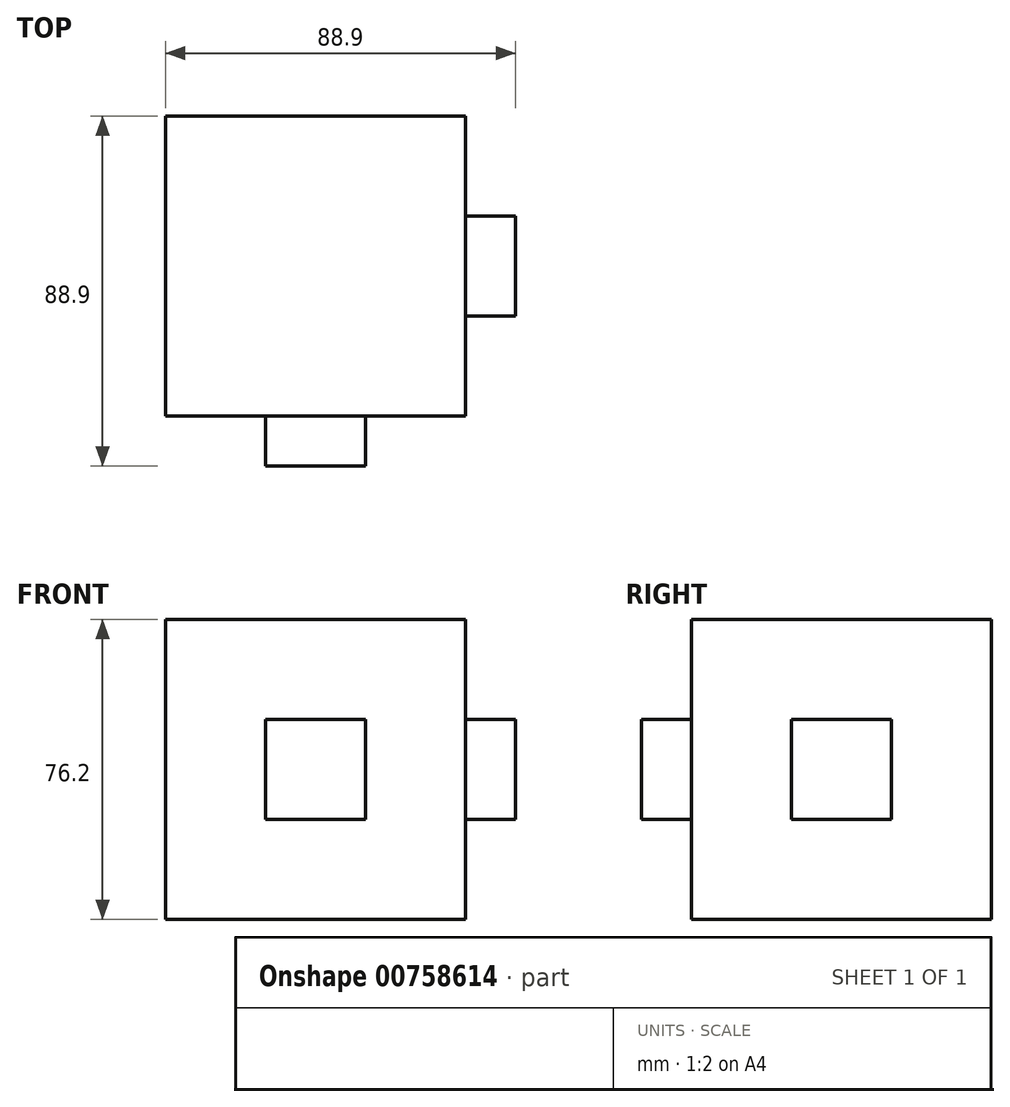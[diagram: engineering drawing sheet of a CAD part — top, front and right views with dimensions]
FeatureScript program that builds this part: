
annotation { "Feature Type Name" : "Feature", "Feature Type Description" : "" }
export const myFeature = defineFeature(function(context is Context, id is Id, definition is map)
    precondition{}
    {
        {
            var Q0;
            Q0=qCreatedBy(makeId("Front.planeOp"),FACE);
            var sketch = newSketch(context, id + "F0", { "sketchPlane" : qUnion([Q0])});
            skLineSegment(sketch, "E0.bottom", {"start": v(-42.26, 44.8) * mm, "end": v(33.94, 44.8) * mm});
            skLineSegment(sketch, "E0.top", {"start": v(-42.26, -31.4) * mm, "end": v(33.94, -31.4) * mm});
            skLineSegment(sketch, "E0.left", {"start": v(-42.26, 44.8) * mm, "end": v(-42.26, -31.4) * mm});
            skLineSegment(sketch, "E0.right", {"start": v(33.94, 44.8) * mm, "end": v(33.94, -31.4) * mm});
            skSolve(sketch);
        }
        {
            var Q0;
            Q0=makeQuery(id+"F0.imprint","IMPRINT",FACE,{"disambiguationData":[TD([[makeQuery(id+"F0.imprint","IMPRINT",EDGE,{"derivedFrom":sQuery(id+"F0.wireOp",EDGE,"E0.bottom")}),-1.0]])]});
            extrude(context, id + "F1", {"entities" : qUnion([Q0]), "depth" : 76.2 * mm, "offsetDistance" : 25.4 * mm});
        }
        {
            var Q0;
            Q0=makeQuery(id+"F1.opExtrude","CAP_FACE",FACE,{"disambiguationData":[OSD([sQuery(id+"F0.wireOp",EDGE,"E0.bottom"),sQuery(id+"F0.wireOp",EDGE,"E0.top"),sQuery(id+"F0.wireOp",EDGE,"E0.left"),sQuery(id+"F0.wireOp",EDGE,"E0.right")])],"isStart":false});
            var sketch = newSketch(context, id + "F2", { "sketchPlane" : qUnion([Q0])});
            skLineSegment(sketch, "E1.bottom", {"start": v(-16.86, 19.4) * mm, "end": v(8.54, 19.4) * mm});
            skLineSegment(sketch, "E1.top", {"start": v(-16.86, -6) * mm, "end": v(8.54, -6) * mm});
            skLineSegment(sketch, "E1.left", {"start": v(-16.86, 19.4) * mm, "end": v(-16.86, -6) * mm});
            skLineSegment(sketch, "E1.right", {"start": v(8.54, 19.4) * mm, "end": v(8.54, -6) * mm});
            skSolve(sketch);
        }
        {
            var Q0;
            Q0=makeQuery(id+"F2.imprint","IMPRINT",FACE,{"disambiguationData":[TD([[makeQuery(id+"F2.imprint","IMPRINT",EDGE,{"derivedFrom":sQuery(id+"F2.wireOp",EDGE,"E1.bottom")}),-1.0]])]});
            extrude(context, id + "F3", {"entities" : qUnion([Q0]), "operationType" : NewBodyOperationType.ADD, "depth" : 12.7 * mm, "offsetDistance" : 25.4 * mm});
        }
        {
            var Q0;
            Q0=makeQuery(id+"F1.opExtrude","SWEPT_FACE",FACE,{"disambiguationData":[OSD([sQuery(id+"F0.wireOp",EDGE,"E0.right")])]});
            var sketch = newSketch(context, id + "F4", { "sketchPlane" : qUnion([Q0])});
            skLineSegment(sketch, "E2.bottom", {"start": v(-50.8, 19.4) * mm, "end": v(-25.4, 19.4) * mm});
            skLineSegment(sketch, "E2.top", {"start": v(-50.8, -6) * mm, "end": v(-25.4, -6) * mm});
            skLineSegment(sketch, "E2.left", {"start": v(-50.8, 19.4) * mm, "end": v(-50.8, -6) * mm});
            skLineSegment(sketch, "E2.right", {"start": v(-25.4, 19.4) * mm, "end": v(-25.4, -6) * mm});
            skSolve(sketch);
        }
        {
            var Q0;
            Q0=makeQuery(id+"F4.imprint","IMPRINT",FACE,{"disambiguationData":[TD([[makeQuery(id+"F4.imprint","IMPRINT",EDGE,{"derivedFrom":sQuery(id+"F4.wireOp",EDGE,"E2.bottom")}),-1.0]])]});
            extrude(context, id + "F5", {"entities" : qUnion([Q0]), "operationType" : NewBodyOperationType.ADD, "depth" : 12.7 * mm, "offsetDistance" : 25.4 * mm});
        }
    });
